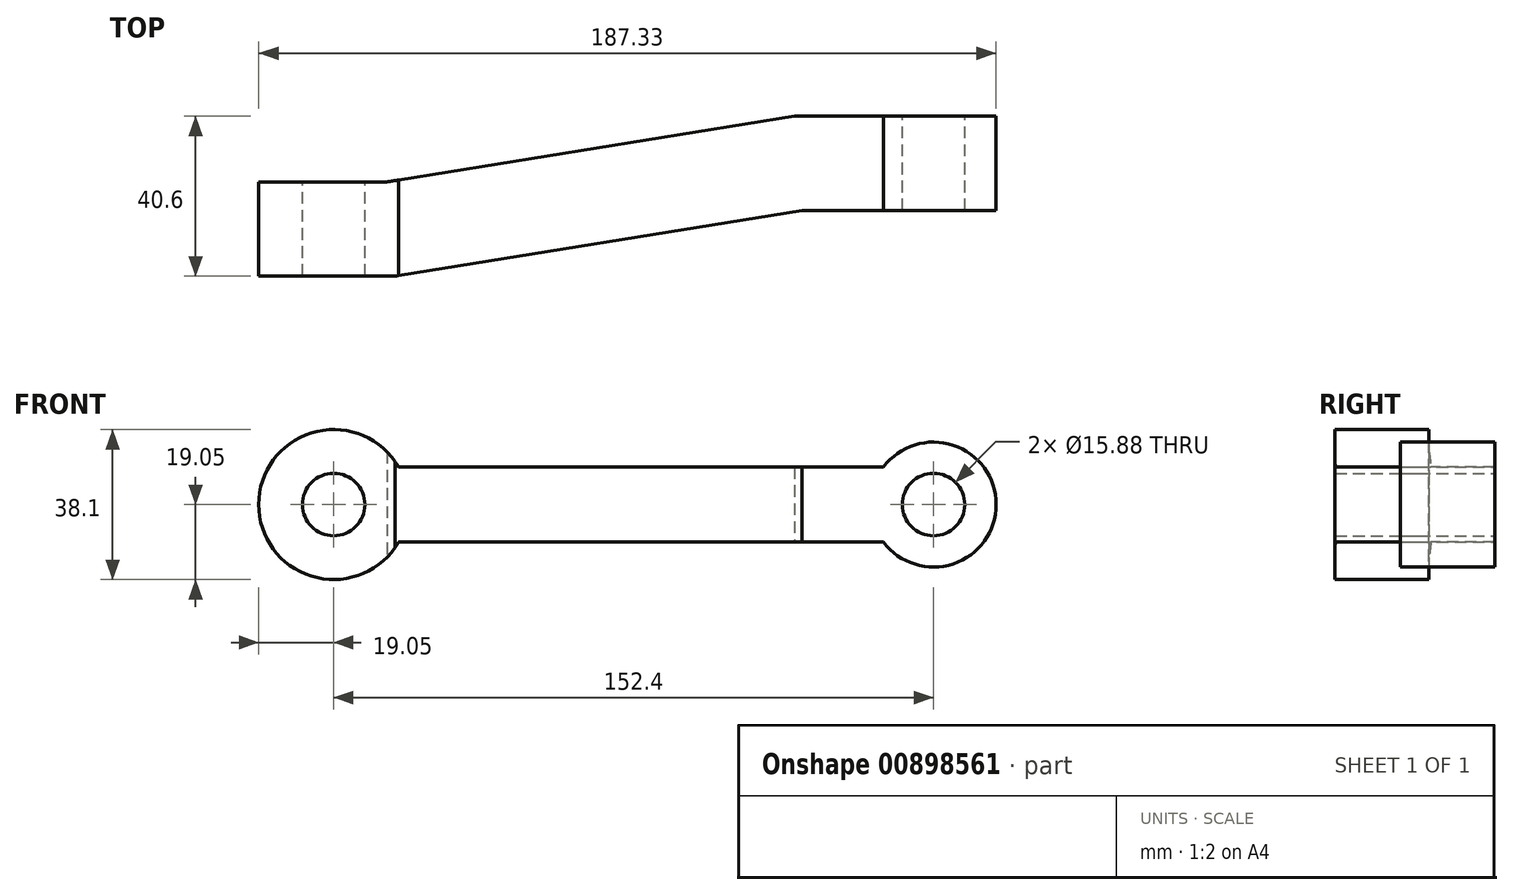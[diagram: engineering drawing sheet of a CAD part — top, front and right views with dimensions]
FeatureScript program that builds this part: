
annotation { "Feature Type Name" : "Feature", "Feature Type Description" : "" }
export const myFeature = defineFeature(function(context is Context, id is Id, definition is map)
    precondition{}
    {
        {
            var Q0;
            Q0=qCreatedBy(makeId("Front.planeOp"),FACE);
            var sketch = newSketch(context, id + "F0", { "sketchPlane" : qUnion([Q0])});
            skCircle(sketch, "E0", {"center": v(0, 0) * mm, "radius": 19.05 * mm});
            skCircle(sketch, "E1", {"center": v(152.4, 0) * mm, "radius": 15.88 * mm});
            skLineSegment(sketch, "E2", {"start": v(0, 0) * mm, "end": v(152.4, 0) * mm, "construction": true});
            skLineSegment(sketch, "E3", {"start": v(16.5, 9.53) * mm, "end": v(139.7, 9.53) * mm});
            skLineSegment(sketch, "E4.MirrorCS", {"start": v(16.5, -9.53) * mm, "end": v(139.7, -9.53) * mm});
            skCircle(sketch, "E5", {"center": v(0, 0) * mm, "radius": 7.94 * mm});
            skCircle(sketch, "E6", {"center": v(152.4, 0) * mm, "radius": 7.94 * mm});
            skSolve(sketch);
        }
        {
            var Q0;
            Q0 = qSketchRegion(id + "F0", true);
            extrude(context, id + "F1", {"entities" : qUnion([Q0]), "endBound" : BoundingType.SYMMETRIC, "depth" : 46.74 * mm, "offsetDistance" : 25.4 * mm});
        }
        {
            var Q0;
            Q0=qCreatedBy(makeId("Top.planeOp"),FACE);
            var sketch = newSketch(context, id + "F2", { "sketchPlane" : qUnion([Q0])});
            skLineSegment(sketch, "E7", {"start": v(-19.05, -23.4) * mm, "end": v(15.48, -23.4) * mm});
            skLineSegment(sketch, "E8", {"start": v(15.48, -23.4) * mm, "end": v(119, -6.73) * mm});
            skLineSegment(sketch, "E9", {"start": v(119, -6.73) * mm, "end": v(168.28, -6.73) * mm});
            skLineSegment(sketch, "E10.0", {"start": v(117.09, 17.23) * mm, "end": v(168.28, 17.23) * mm});
            skLineSegment(sketch, "E10.1", {"start": v(13.56, 0.57) * mm, "end": v(117.09, 17.23) * mm});
            skLineSegment(sketch, "E10.2", {"start": v(-19.05, 0.57) * mm, "end": v(13.56, 0.57) * mm});
            skLineSegment(sketch, "E11", {"start": v(168.28, -6.73) * mm, "end": v(168.28, 17.23) * mm});
            skLineSegment(sketch, "E12", {"start": v(168.28, 23.37) * mm, "end": v(168.28, -23.37) * mm});
            skLineSegment(sketch, "E13", {"start": v(-19.05, -23.4) * mm, "end": v(-19.05, -18.54) * mm});
            skLineSegment(sketch, "E14", {"start": v(-19.05, -23.4) * mm, "end": v(-19.05, 0.57) * mm});
            skLineSegment(sketch, "E15", {"start": v(-19.05, -23.37) * mm, "end": v(-19.05, 23.37) * mm});
            skSolve(sketch);
        }
        {
            var Q0;
            Q0 = qSketchRegion(id + "F2", true);
            extrude(context, id + "F3", {"entities" : qUnion([Q0]), "operationType" : NewBodyOperationType.INTERSECT, "endBound" : BoundingType.SYMMETRIC, "depth" : 50.8 * mm, "offsetDistance" : 25.4 * mm});
        }
    });
